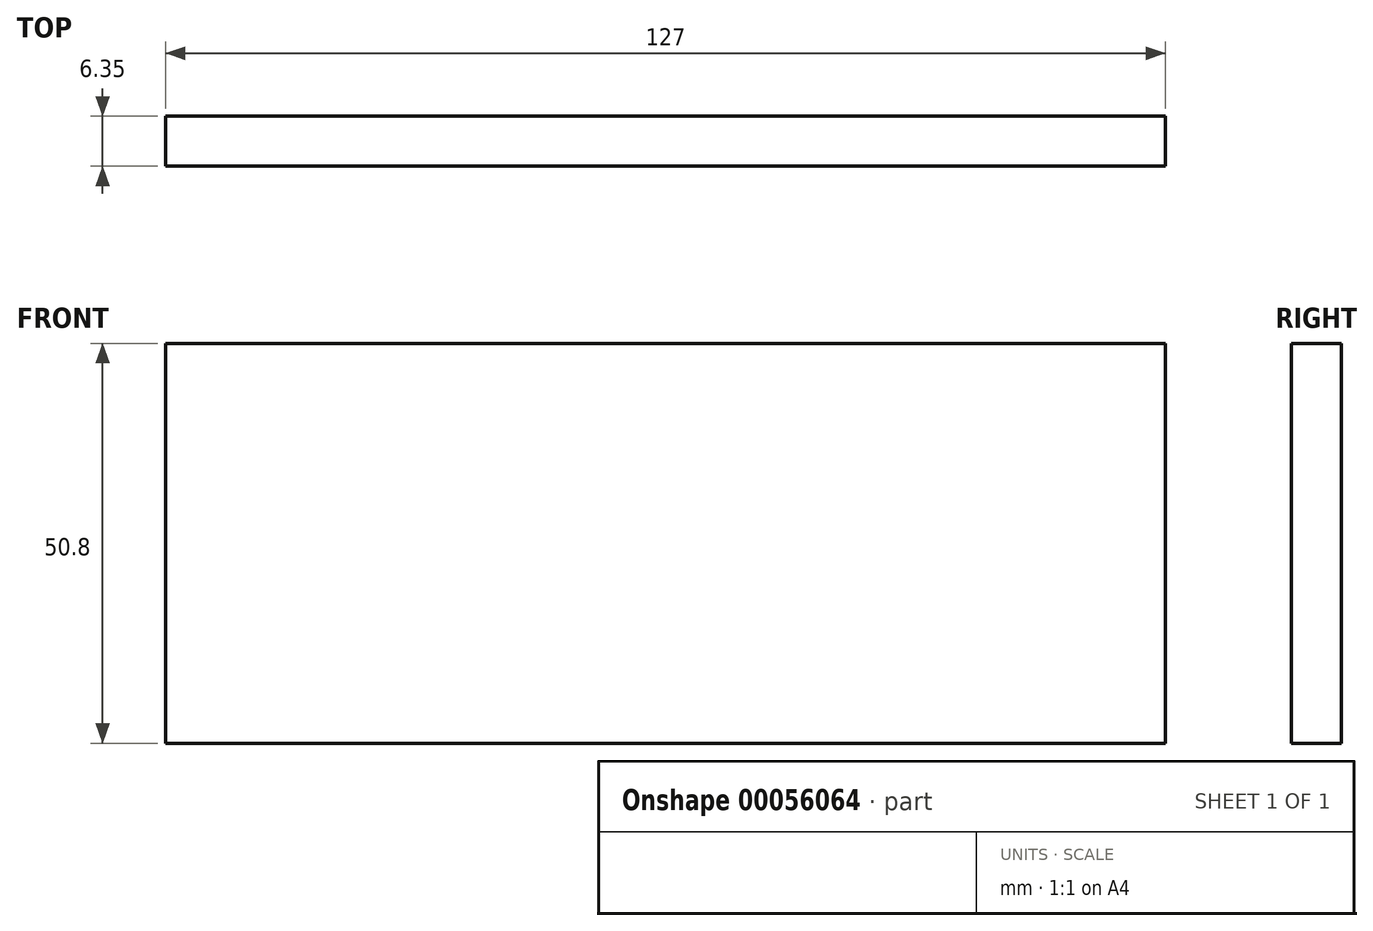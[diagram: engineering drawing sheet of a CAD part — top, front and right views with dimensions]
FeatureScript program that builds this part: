
annotation { "Feature Type Name" : "Feature", "Feature Type Description" : "" }
export const myFeature = defineFeature(function(context is Context, id is Id, definition is map)
    precondition{}
    {
        {
            var Q0;
            Q0=qCreatedBy(makeId("Front.planeOp"),FACE);
            var sketch = newSketch(context, id + "F0", { "sketchPlane" : qUnion([Q0])});
            skLineSegment(sketch, "E0.bottom", {"start": v(-65.35, 75.56) * mm, "end": v(61.65, 75.56) * mm});
            skLineSegment(sketch, "E0.top", {"start": v(-65.35, 24.76) * mm, "end": v(61.65, 24.76) * mm});
            skLineSegment(sketch, "E0.left", {"start": v(-65.35, 75.56) * mm, "end": v(-65.35, 24.76) * mm});
            skLineSegment(sketch, "E0.right", {"start": v(61.65, 75.56) * mm, "end": v(61.65, 24.76) * mm});
            skSolve(sketch);
        }
        {
            var Q0;
            Q0=makeQuery(id+"F0.imprint","IMPRINT",FACE,{"disambiguationData":[TD([[makeQuery(id+"F0.imprint","IMPRINT",EDGE,{"derivedFrom":sQuery(id+"F0.wireOp",EDGE,"E0.bottom")}),-1.0]])]});
            extrude(context, id + "F1", {"entities" : qUnion([Q0]), "depth" : 6.35 * mm});
        }
    });
